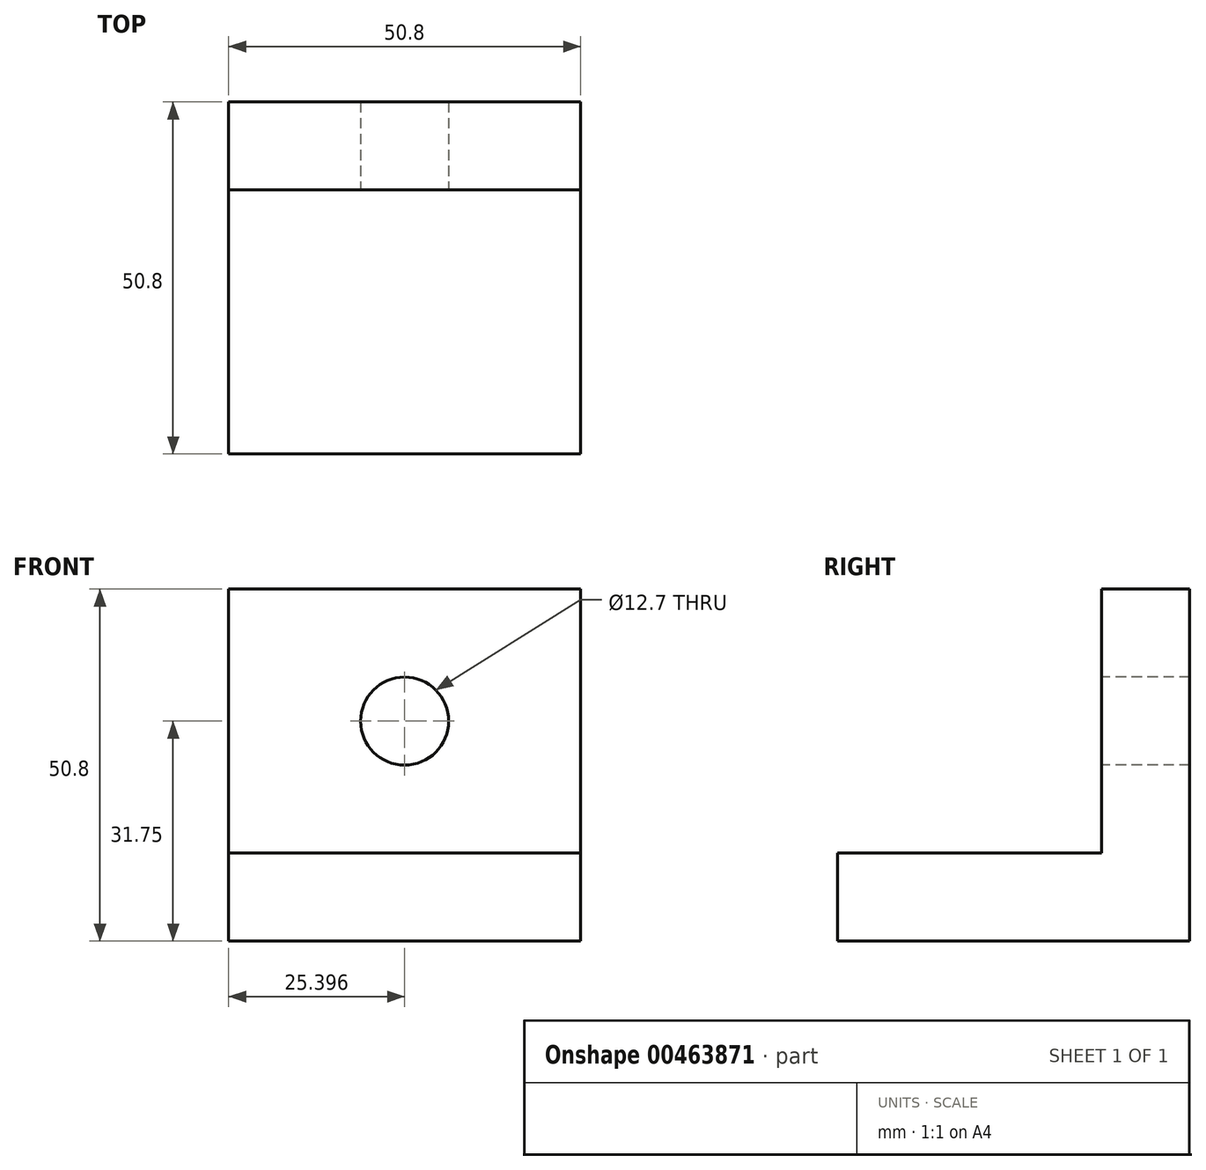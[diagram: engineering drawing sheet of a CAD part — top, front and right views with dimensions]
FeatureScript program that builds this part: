
annotation { "Feature Type Name" : "Feature", "Feature Type Description" : "" }
export const myFeature = defineFeature(function(context is Context, id is Id, definition is map)
    precondition{}
    {
        {
            var Q0;
            Q0=qCreatedBy(makeId("Top.planeOp"),FACE);
            var sketch = newSketch(context, id + "F0", { "sketchPlane" : qUnion([Q0])});
            skLineSegment(sketch, "E0.bottom", {"start": v(-23.84, 21.92) * mm, "end": v(26.96, 21.92) * mm});
            skLineSegment(sketch, "E0.top", {"start": v(-23.84, -28.88) * mm, "end": v(26.96, -28.88) * mm});
            skLineSegment(sketch, "E0.left", {"start": v(-23.84, 21.92) * mm, "end": v(-23.84, -28.88) * mm});
            skLineSegment(sketch, "E0.right", {"start": v(26.96, 21.92) * mm, "end": v(26.96, -28.88) * mm});
            skSolve(sketch);
        }
        {
            var Q0;
            Q0 = qSketchRegion(id + "F0", true);
            extrude(context, id + "F1", {"entities" : qUnion([Q0]), "depth" : 12.7 * mm});
        }
        {
            var Q0;
            Q0=makeQuery(id+"F1.opExtrude","CAP_FACE",FACE,{"disambiguationData":[OSD([sQuery(id+"F0.wireOp",EDGE,"E0.bottom"),sQuery(id+"F0.wireOp",EDGE,"E0.top"),sQuery(id+"F0.wireOp",EDGE,"E0.left"),sQuery(id+"F0.wireOp",EDGE,"E0.right")])],"isStart":false});
            var sketch = newSketch(context, id + "F2", { "sketchPlane" : qUnion([Q0])});
            skLineSegment(sketch, "E1.bottom", {"start": v(-23.84, 21.92) * mm, "end": v(26.96, 21.92) * mm});
            skLineSegment(sketch, "E1.top", {"start": v(-23.84, 9.22) * mm, "end": v(26.96, 9.22) * mm});
            skLineSegment(sketch, "E1.left", {"start": v(-23.84, 21.92) * mm, "end": v(-23.84, 9.22) * mm});
            skLineSegment(sketch, "E1.right", {"start": v(26.96, 21.92) * mm, "end": v(26.96, 9.22) * mm});
            skSolve(sketch);
        }
        {
            var Q0;
            Q0 = qSketchRegion(id + "F2", true);
            extrude(context, id + "F3", {"entities" : qUnion([Q0]), "operationType" : NewBodyOperationType.ADD, "depth" : 38.1 * mm});
        }
        {
            var Q0;
            Q0=makeQuery(id+"F3.opExtrude","SWEPT_FACE",FACE,{"disambiguationData":[OSD([sQuery(id+"F2.wireOp",EDGE,"E1.top")])]});
            var sketch = newSketch(context, id + "F4", { "sketchPlane" : qUnion([Q0])});
            skCircle(sketch, "E2", {"center": v(1.56, 31.75) * mm, "radius": 6.35 * mm});
            skPoint(sketch, "E2.centerSnap0", {"position": v(1.56, 50.8) * mm});
            skPoint(sketch, "E2.centerSnap1", {"position": v(-23.84, 31.75) * mm});
            skSolve(sketch);
        }
        {
            var Q0;
            Q0 = qSketchRegion(id + "F4", true);
            extrude(context, id + "F5", {"entities" : qUnion([Q0]), "operationType" : NewBodyOperationType.REMOVE, "oppositeDirection" : true, "depth" : 25.4 * mm});
        }
    });
